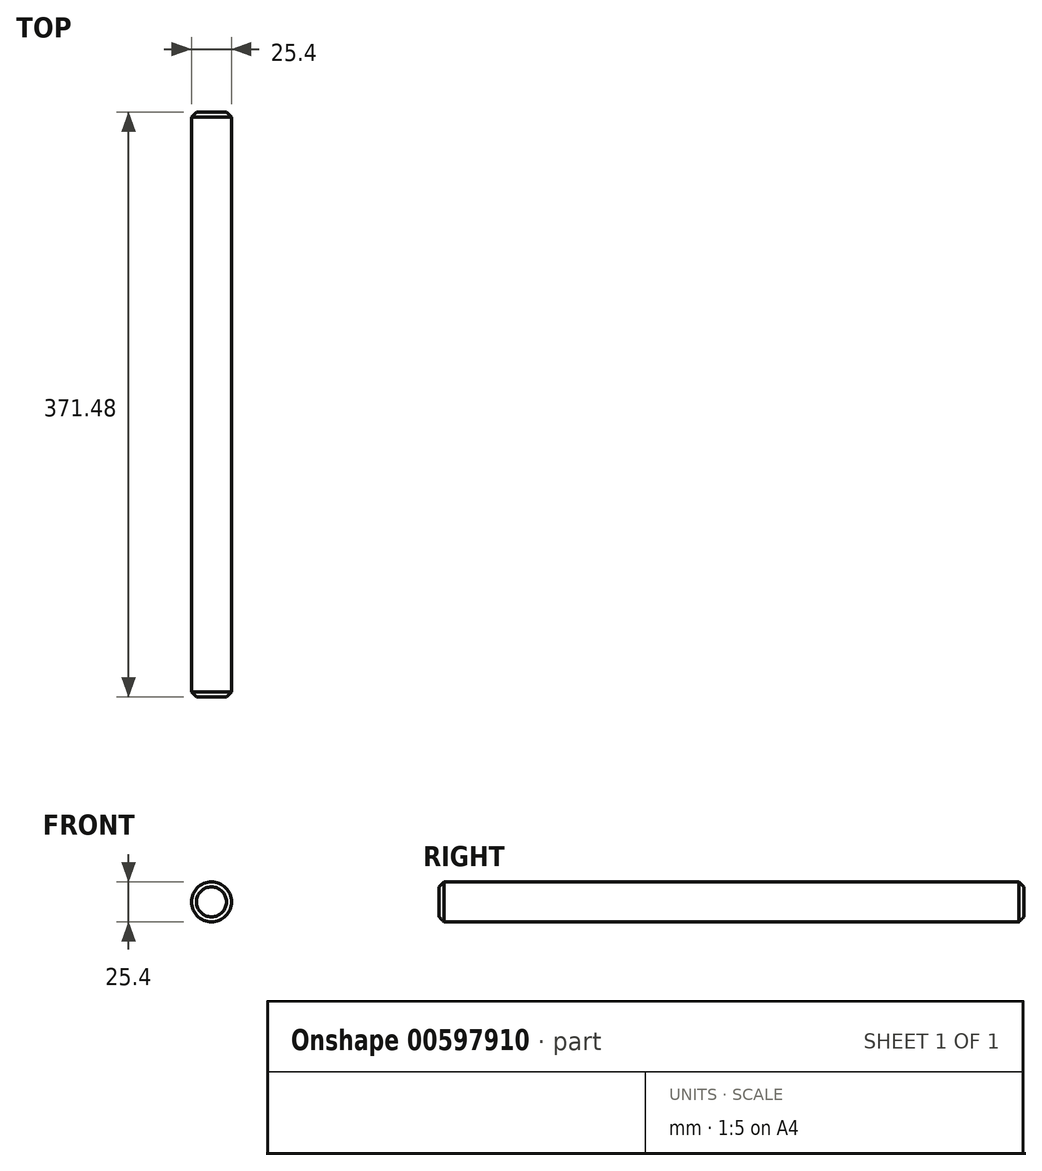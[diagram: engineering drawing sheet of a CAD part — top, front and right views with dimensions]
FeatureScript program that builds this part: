
annotation { "Feature Type Name" : "Feature", "Feature Type Description" : "" }
export const myFeature = defineFeature(function(context is Context, id is Id, definition is map)
    precondition{}
    {
        {
            var Q0;
            Q0=qCreatedBy(makeId("Front.planeOp"),FACE);
            var sketch = newSketch(context, id + "F0", { "sketchPlane" : qUnion([Q0])});
            skCircle(sketch, "E0", {"center": v(0, 0) * mm, "radius": 12.7 * mm});
            skSolve(sketch);
        }
        {
            var Q0;
            Q0 = qSketchRegion(id + "F0", true);
            extrude(context, id + "F1", {"entities" : qUnion([Q0]), "depth" : 371.47 * mm, "offsetDistance" : 25.4 * mm});
        }
        {
            var Q0;
            Q0=makeQuery(id+"F1.opExtrude","CAP_EDGE",EDGE,{"disambiguationData":[OSD([sQuery(id+"F0.wireOp",EDGE,"E0")])],"isStart":true});
            var Q1;
            Q1=makeQuery(id+"F1.opExtrude","CAP_EDGE",EDGE,{"disambiguationData":[OSD([sQuery(id+"F0.wireOp",EDGE,"E0")])],"isStart":false});
            chamfer(context, id + "F2", {"entities" : qUnion([Q0, Q1]), "width" : 3.17 * mm, "tangentPropagation" : true});
        }
    });
